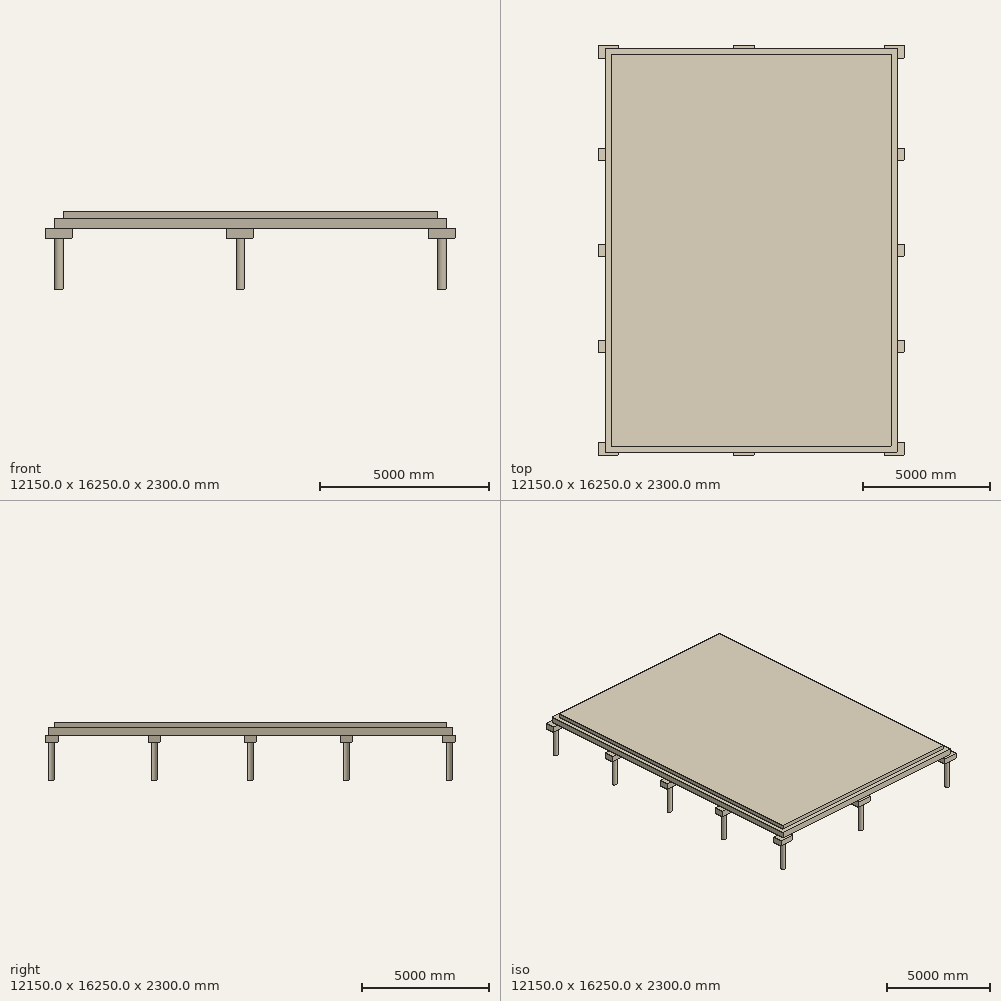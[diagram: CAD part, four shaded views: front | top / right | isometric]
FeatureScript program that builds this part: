
annotation { "Feature Type Name" : "Feature", "Feature Type Description" : "" }
export const myFeature = defineFeature(function(context is Context, id is Id, definition is map)
    precondition{}
    {
        {
            var Q0;
            Q0=qCreatedBy(makeId("Top.planeOp"),FACE);
            var sketch = newSketch(context, id + "F0", { "sketchPlane" : qUnion([Q0])});
            skLineSegment(sketch, "E0.bottom", {"start": v(5550, 7750) * mm, "end": v(-5550, 7750) * mm, "construction": true});
            skLineSegment(sketch, "E0.top", {"start": v(5550, -7750) * mm, "end": v(-5550, -7750) * mm, "construction": true});
            skLineSegment(sketch, "E0.left", {"start": v(5550, 7750) * mm, "end": v(5550, -7750) * mm, "construction": true});
            skLineSegment(sketch, "E0.right", {"start": v(-5550, 7750) * mm, "end": v(-5550, -7750) * mm, "construction": true});
            skPoint(sketch, "E0.middle", {"position": v(0, 0) * mm});
            skLineSegment(sketch, "E1", {"start": v(-300, -7750) * mm, "end": v(-300, 7750) * mm, "construction": true});
            skPoint(sketch, "E2", {"position": v(-5550, 0) * mm});
            skPoint(sketch, "E3", {"position": v(-5550, 3800) * mm});
            skPoint(sketch, "E4", {"position": v(-5550, -3800) * mm});
            skPoint(sketch, "E5", {"position": v(5550, -3800) * mm});
            skPoint(sketch, "E6", {"position": v(5550, 0) * mm});
            skPoint(sketch, "E7", {"position": v(5550, 3800) * mm});
            skLineSegment(sketch, "E8", {"start": v(900, 7750) * mm, "end": v(900, -7750) * mm, "construction": true});
            skLineSegment(sketch, "E9", {"start": v(5550, 3800) * mm, "end": v(900, 3800) * mm, "construction": true});
            skLineSegment(sketch, "E10", {"start": v(5550, 0) * mm, "end": v(900, 0) * mm, "construction": true});
            skLineSegment(sketch, "E11", {"start": v(5550, -3800) * mm, "end": v(900, -3800) * mm, "construction": true});
            skLineSegment(sketch, "E12", {"start": v(5550, 4900) * mm, "end": v(2550, 4900) * mm, "construction": true});
            skLineSegment(sketch, "E13", {"start": v(2550, 4900) * mm, "end": v(2550, 2700) * mm, "construction": true});
            skLineSegment(sketch, "E14", {"start": v(2550, -4900) * mm, "end": v(5550, -4900) * mm, "construction": true});
            skLineSegment(sketch, "E15", {"start": v(-4350, 7750) * mm, "end": v(-4350, 1750) * mm, "construction": true});
            skLineSegment(sketch, "E16", {"start": v(-4350, 1750) * mm, "end": v(-300, 1750) * mm, "construction": true});
            skLineSegment(sketch, "E17", {"start": v(-4350, 4750) * mm, "end": v(-3250, 4750) * mm, "construction": true});
            skLineSegment(sketch, "E18", {"start": v(-3250, 4750) * mm, "end": v(-3250, 7750) * mm, "construction": true});
            skLineSegment(sketch, "E19", {"start": v(-5550, 0) * mm, "end": v(-2550, 0) * mm, "construction": true});
            skLineSegment(sketch, "E20", {"start": v(-2550, 0) * mm, "end": v(-2550, -3800) * mm, "construction": true});
            skLineSegment(sketch, "E21", {"start": v(-2550, -3800) * mm, "end": v(-5550, -3800) * mm, "construction": true});
            skLineSegment(sketch, "E22", {"start": v(-5550, -2700) * mm, "end": v(-2550, -2700) * mm, "construction": true});
            skLineSegment(sketch, "E23", {"start": v(2550, 2700) * mm, "end": v(5550, 2700) * mm, "construction": true});
            skLineSegment(sketch, "E24", {"start": v(2550, -2700) * mm, "end": v(5550, -2700) * mm, "construction": true});
            skLineSegment(sketch, "E25.trimOffspring", {"start": v(2550, -2700) * mm, "end": v(2550, -4900) * mm, "construction": true});
            skPoint(sketch, "E26", {"position": v(-300, 0) * mm});
            skPoint(sketch, "E27", {"position": v(-300, 3800) * mm});
            skPoint(sketch, "E28", {"position": v(-300, -3800) * mm});
            skSolve(sketch);
        }
        {
            var Q0;
            Q0=qCreatedBy(makeId("Top.planeOp"),FACE);
            var sketch = newSketch(context, id + "F1", { "sketchPlane" : qUnion([Q0])});
            skLineSegment(sketch, "E29.0", {"start": v(5550, -7750) * mm, "end": v(-175, -7750) * mm});
            skLineSegment(sketch, "E30.0", {"start": v(-5550, 7750) * mm, "end": v(-5550, -7750) * mm});
            skLineSegment(sketch, "E31.0", {"start": v(5550, 7750) * mm, "end": v(-175, 7750) * mm});
            skLineSegment(sketch, "E32.0", {"start": v(5550, 7750) * mm, "end": v(5550, -7750) * mm});
            skLineSegment(sketch, "E33.0", {"start": v(-300, -7750) * mm, "end": v(-300, 7750) * mm, "construction": true});
            skLineSegment(sketch, "E34.0", {"start": v(5800, -8000) * mm, "end": v(-5800, -8000) * mm});
            skLineSegment(sketch, "E34.1", {"start": v(5800, 8000) * mm, "end": v(5800, -8000) * mm});
            skLineSegment(sketch, "E34.2", {"start": v(5800, 8000) * mm, "end": v(-5800, 8000) * mm});
            skLineSegment(sketch, "E34.3", {"start": v(-5800, 8000) * mm, "end": v(-5800, -8000) * mm});
            skLineSegment(sketch, "E35.left", {"start": v(-425, 7750) * mm, "end": v(-425, -7750) * mm});
            skLineSegment(sketch, "E35.right", {"start": v(-175, 7750) * mm, "end": v(-175, -7750) * mm});
            skPoint(sketch, "E35.middle", {"position": v(-300, 0) * mm});
            skLineSegment(sketch, "E36.trimOffspring", {"start": v(-425, -7750) * mm, "end": v(-5550, -7750) * mm});
            skLineSegment(sketch, "E37.trimOffspring", {"start": v(-425, 7750) * mm, "end": v(-5550, 7750) * mm});
            skLineSegment(sketch, "E38", {"start": v(-5800, -8000) * mm, "end": v(-5550, -7750) * mm, "construction": true});
            skPoint(sketch, "E39", {"position": v(-5675, -7875) * mm});
            skSolve(sketch);
        }
        {
            var Q0;
            Q0 = qSketchRegion(id + "F1", true);
            extrude(context, id + "F2", {"entities" : qUnion([Q0]), "oppositeDirection" : true, "depth" : 300 * mm});
        }
        {
            var Q0;
            Q0=makeQuery(id+"F2.opExtrude","CAP_FACE",FACE,{"disambiguationData":[OSD([sQuery(id+"F1.wireOp",EDGE,"E29.0"),sQuery(id+"F1.wireOp",EDGE,"E30.0"),sQuery(id+"F1.wireOp",EDGE,"E31.0"),sQuery(id+"F1.wireOp",EDGE,"E32.0"),sQuery(id+"F1.wireOp",EDGE,"E34.0"),sQuery(id+"F1.wireOp",EDGE,"E34.1"),sQuery(id+"F1.wireOp",EDGE,"E34.2"),sQuery(id+"F1.wireOp",EDGE,"E34.3"),sQuery(id+"F1.wireOp",EDGE,"E35.left"),sQuery(id+"F1.wireOp",EDGE,"E35.right"),sQuery(id+"F1.wireOp",EDGE,"E36.trimOffspring"),sQuery(id+"F1.wireOp",EDGE,"E37.trimOffspring")])],"isStart":false});
            var sketch = newSketch(context, id + "F3", { "sketchPlane" : qUnion([Q0])});
            skLineSegment(sketch, "E40", {"start": v(-5800, -8000) * mm, "end": v(-5550, -7750) * mm, "construction": true});
            skLineSegment(sketch, "E41", {"start": v(-175, -7750) * mm, "end": v(-425, -8000) * mm, "construction": true});
            skLineSegment(sketch, "E42", {"start": v(-425, 7750) * mm, "end": v(-175, 8000) * mm, "construction": true});
            skLineSegment(sketch, "E43", {"start": v(-5800, 8000) * mm, "end": v(-5550, 7750) * mm, "construction": true});
            skLineSegment(sketch, "E44", {"start": v(5800, 8000) * mm, "end": v(5550, 7750) * mm, "construction": true});
            skLineSegment(sketch, "E45", {"start": v(5550, -7750) * mm, "end": v(5800, -8000) * mm, "construction": true});
            skPoint(sketch, "E46.0", {"position": v(-5550, 0) * mm});
            skPoint(sketch, "E47.0", {"position": v(-5550, -3800) * mm});
            skPoint(sketch, "E48.0", {"position": v(-300, -3800) * mm});
            skPoint(sketch, "E49.0", {"position": v(-300, 0) * mm});
            skPoint(sketch, "E50.0", {"position": v(5550, -3800) * mm});
            skPoint(sketch, "E51.0", {"position": v(5550, 0) * mm});
            skPoint(sketch, "E52.0", {"position": v(5550, 3800) * mm});
            skPoint(sketch, "E53.0", {"position": v(-300, 3800) * mm});
            skPoint(sketch, "E54.0", {"position": v(-5550, 3800) * mm});
            skLineSegment(sketch, "E55", {"start": v(-5550, 3800) * mm, "end": v(-5800, 3800) * mm, "construction": true});
            skLineSegment(sketch, "E56", {"start": v(-5550, 0) * mm, "end": v(-5800, 0) * mm, "construction": true});
            skLineSegment(sketch, "E57", {"start": v(5550, 0) * mm, "end": v(5800, 0) * mm, "construction": true});
            skLineSegment(sketch, "E58", {"start": v(5550, 3800) * mm, "end": v(5800, 3800) * mm, "construction": true});
            skLineSegment(sketch, "E59", {"start": v(-5550, -3800) * mm, "end": v(-5800, -3800) * mm, "construction": true});
            skLineSegment(sketch, "E60", {"start": v(5550, -3800) * mm, "end": v(5800, -3800) * mm, "construction": true});
            skLineSegment(sketch, "E61.bottom", {"start": v(-5275, 8125) * mm, "end": v(-6075, 8125) * mm});
            skLineSegment(sketch, "E61.top", {"start": v(-5275, 7625) * mm, "end": v(-6075, 7625) * mm});
            skLineSegment(sketch, "E61.left", {"start": v(-5275, 8125) * mm, "end": v(-5275, 7625) * mm});
            skLineSegment(sketch, "E61.right", {"start": v(-6075, 8125) * mm, "end": v(-6075, 7625) * mm});
            skPoint(sketch, "E61.middle", {"position": v(-5675, 7875) * mm});
            skLineSegment(sketch, "E62.bottom", {"start": v(-5275, 4050) * mm, "end": v(-6075, 4050) * mm});
            skLineSegment(sketch, "E62.top", {"start": v(-5275, 3550) * mm, "end": v(-6075, 3550) * mm});
            skLineSegment(sketch, "E62.left", {"start": v(-5275, 4050) * mm, "end": v(-5275, 3550) * mm});
            skLineSegment(sketch, "E62.right", {"start": v(-6075, 4050) * mm, "end": v(-6075, 3550) * mm});
            skPoint(sketch, "E62.middle", {"position": v(-5675, 3800) * mm});
            skLineSegment(sketch, "E63.bottom", {"start": v(-5275, 250) * mm, "end": v(-6075, 250) * mm});
            skLineSegment(sketch, "E63.top", {"start": v(-5275, -250) * mm, "end": v(-6075, -250) * mm});
            skLineSegment(sketch, "E63.left", {"start": v(-5275, 250) * mm, "end": v(-5275, -250) * mm});
            skLineSegment(sketch, "E63.right", {"start": v(-6075, 250) * mm, "end": v(-6075, -250) * mm});
            skPoint(sketch, "E63.middle", {"position": v(-5675, 0) * mm});
            skLineSegment(sketch, "E64.bottom", {"start": v(-6075, -3550) * mm, "end": v(-5275, -3550) * mm});
            skLineSegment(sketch, "E64.top", {"start": v(-6075, -4050) * mm, "end": v(-5275, -4050) * mm});
            skLineSegment(sketch, "E64.left", {"start": v(-6075, -3550) * mm, "end": v(-6075, -4050) * mm});
            skLineSegment(sketch, "E64.right", {"start": v(-5275, -3550) * mm, "end": v(-5275, -4050) * mm});
            skPoint(sketch, "E64.middle", {"position": v(-5675, -3800) * mm});
            skLineSegment(sketch, "E65.bottom", {"start": v(-5275, -7625) * mm, "end": v(-6075, -7625) * mm});
            skLineSegment(sketch, "E65.top", {"start": v(-5275, -8125) * mm, "end": v(-6075, -8125) * mm});
            skLineSegment(sketch, "E65.left", {"start": v(-5275, -7625) * mm, "end": v(-5275, -8125) * mm});
            skLineSegment(sketch, "E65.right", {"start": v(-6075, -7625) * mm, "end": v(-6075, -8125) * mm});
            skPoint(sketch, "E65.middle", {"position": v(-5675, -7875) * mm});
            skLineSegment(sketch, "E66.bottom", {"start": v(100, 8125) * mm, "end": v(-700, 8125) * mm});
            skLineSegment(sketch, "E66.top", {"start": v(100, 7625) * mm, "end": v(-700, 7625) * mm});
            skLineSegment(sketch, "E66.left", {"start": v(100, 8125) * mm, "end": v(100, 7625) * mm});
            skLineSegment(sketch, "E66.right", {"start": v(-700, 8125) * mm, "end": v(-700, 7625) * mm});
            skPoint(sketch, "E66.middle", {"position": v(-300, 7875) * mm});
            skLineSegment(sketch, "E67.bottom", {"start": v(6075, 8125) * mm, "end": v(5275, 8125) * mm});
            skLineSegment(sketch, "E67.top", {"start": v(6075, 7625) * mm, "end": v(5275, 7625) * mm});
            skLineSegment(sketch, "E67.left", {"start": v(6075, 8125) * mm, "end": v(6075, 7625) * mm});
            skLineSegment(sketch, "E67.right", {"start": v(5275, 8125) * mm, "end": v(5275, 7625) * mm});
            skPoint(sketch, "E67.middle", {"position": v(5675, 7875) * mm});
            skLineSegment(sketch, "E68.bottom", {"start": v(100, 4050) * mm, "end": v(-700, 4050) * mm});
            skLineSegment(sketch, "E68.top", {"start": v(100, 3550) * mm, "end": v(-700, 3550) * mm});
            skLineSegment(sketch, "E68.left", {"start": v(100, 4050) * mm, "end": v(100, 3550) * mm});
            skLineSegment(sketch, "E68.right", {"start": v(-700, 4050) * mm, "end": v(-700, 3550) * mm});
            skLineSegment(sketch, "E69.bottom", {"start": v(6075, 4050) * mm, "end": v(5275, 4050) * mm});
            skLineSegment(sketch, "E69.top", {"start": v(6075, 3550) * mm, "end": v(5275, 3550) * mm});
            skLineSegment(sketch, "E69.left", {"start": v(6075, 4050) * mm, "end": v(6075, 3550) * mm});
            skLineSegment(sketch, "E69.right", {"start": v(5275, 4050) * mm, "end": v(5275, 3550) * mm});
            skPoint(sketch, "E69.middle", {"position": v(5675, 3800) * mm});
            skLineSegment(sketch, "E70.bottom", {"start": v(100, 250) * mm, "end": v(-700, 250) * mm});
            skLineSegment(sketch, "E70.top", {"start": v(100, -250) * mm, "end": v(-700, -250) * mm});
            skLineSegment(sketch, "E70.left", {"start": v(100, 250) * mm, "end": v(100, -250) * mm});
            skLineSegment(sketch, "E70.right", {"start": v(-700, 250) * mm, "end": v(-700, -250) * mm});
            skLineSegment(sketch, "E71.bottom", {"start": v(100, -3550) * mm, "end": v(-700, -3550) * mm});
            skLineSegment(sketch, "E71.top", {"start": v(100, -4050) * mm, "end": v(-700, -4050) * mm});
            skLineSegment(sketch, "E71.left", {"start": v(100, -3550) * mm, "end": v(100, -4050) * mm});
            skLineSegment(sketch, "E71.right", {"start": v(-700, -3550) * mm, "end": v(-700, -4050) * mm});
            skLineSegment(sketch, "E72.bottom", {"start": v(100, -7625) * mm, "end": v(-700, -7625) * mm});
            skLineSegment(sketch, "E72.top", {"start": v(100, -8125) * mm, "end": v(-700, -8125) * mm});
            skLineSegment(sketch, "E72.left", {"start": v(100, -7625) * mm, "end": v(100, -8125) * mm});
            skLineSegment(sketch, "E72.right", {"start": v(-700, -7625) * mm, "end": v(-700, -8125) * mm});
            skPoint(sketch, "E72.middle", {"position": v(-300, -7875) * mm});
            skLineSegment(sketch, "E73.bottom", {"start": v(6075, -7625) * mm, "end": v(5275, -7625) * mm});
            skLineSegment(sketch, "E73.top", {"start": v(6075, -8125) * mm, "end": v(5275, -8125) * mm});
            skLineSegment(sketch, "E73.left", {"start": v(6075, -7625) * mm, "end": v(6075, -8125) * mm});
            skLineSegment(sketch, "E73.right", {"start": v(5275, -7625) * mm, "end": v(5275, -8125) * mm});
            skPoint(sketch, "E73.middle", {"position": v(5675, -7875) * mm});
            skLineSegment(sketch, "E74.bottom", {"start": v(6075, -3550) * mm, "end": v(5275, -3550) * mm});
            skLineSegment(sketch, "E74.top", {"start": v(6075, -4050) * mm, "end": v(5275, -4050) * mm});
            skLineSegment(sketch, "E74.left", {"start": v(6075, -3550) * mm, "end": v(6075, -4050) * mm});
            skLineSegment(sketch, "E74.right", {"start": v(5275, -3550) * mm, "end": v(5275, -4050) * mm});
            skPoint(sketch, "E74.middle", {"position": v(5675, -3800) * mm});
            skLineSegment(sketch, "E75.bottom", {"start": v(6075, 250) * mm, "end": v(5275, 250) * mm});
            skLineSegment(sketch, "E75.top", {"start": v(6075, -250) * mm, "end": v(5275, -250) * mm});
            skLineSegment(sketch, "E75.left", {"start": v(6075, 250) * mm, "end": v(6075, -250) * mm});
            skLineSegment(sketch, "E75.right", {"start": v(5275, 250) * mm, "end": v(5275, -250) * mm});
            skPoint(sketch, "E75.middle", {"position": v(5675, 0) * mm});
            skSolve(sketch);
        }
        {
            var Q0;
            Q0 = qSketchRegion(id + "F3", true);
            extrude(context, id + "F4", {"entities" : qUnion([Q0]), "depth" : 300 * mm});
        }
        {
            var Q0;
            Q0=makeQuery(id+"F4.opExtrude","CAP_FACE",FACE,{"disambiguationData":[OSD([sQuery(id+"F3.wireOp",EDGE,"E61.bottom"),sQuery(id+"F3.wireOp",EDGE,"E61.top"),sQuery(id+"F3.wireOp",EDGE,"E61.left"),sQuery(id+"F3.wireOp",EDGE,"E61.right")])],"isStart":false});
            var sketch = newSketch(context, id + "F5", { "sketchPlane" : qUnion([Q0])});
            skPoint(sketch, "E76.0", {"position": v(-5675, -3800) * mm});
            skPoint(sketch, "E77.0", {"position": v(-5675, -7875) * mm});
            skPoint(sketch, "E78.0", {"position": v(-300, -7875) * mm});
            skPoint(sketch, "E79.0", {"position": v(-300, -3800) * mm});
            skPoint(sketch, "E80.0", {"position": v(5675, -3800) * mm});
            skPoint(sketch, "E81.0", {"position": v(5675, -7875) * mm});
            skPoint(sketch, "E82.0", {"position": v(5675, 0) * mm});
            skPoint(sketch, "E83.0", {"position": v(-300, 0) * mm});
            skPoint(sketch, "E84.0", {"position": v(-5675, 0) * mm});
            skPoint(sketch, "E85.0", {"position": v(-5675, 3800) * mm});
            skPoint(sketch, "E86.0", {"position": v(-300, 3800) * mm});
            skPoint(sketch, "E87.0", {"position": v(5675, 3800) * mm});
            skPoint(sketch, "E88.0", {"position": v(5675, 7875) * mm});
            skPoint(sketch, "E89.0", {"position": v(-5675, 7875) * mm});
            skPoint(sketch, "E90.0", {"position": v(-300, 7875) * mm});
            skCircle(sketch, "E91", {"center": v(-5675, 7875) * mm, "radius": 125 * mm});
            skCircle(sketch, "E92", {"center": v(-300, 7875) * mm, "radius": 125 * mm});
            skCircle(sketch, "E93", {"center": v(5675, 7875) * mm, "radius": 125 * mm});
            skCircle(sketch, "E94", {"center": v(-5675, 3800) * mm, "radius": 125 * mm});
            skCircle(sketch, "E95", {"center": v(-300, 3800) * mm, "radius": 125 * mm});
            skCircle(sketch, "E96", {"center": v(5675, 3800) * mm, "radius": 125 * mm});
            skCircle(sketch, "E97", {"center": v(-5675, 0) * mm, "radius": 125 * mm});
            skCircle(sketch, "E98", {"center": v(-300, 0) * mm, "radius": 125 * mm});
            skCircle(sketch, "E99", {"center": v(5675, 0) * mm, "radius": 125 * mm});
            skCircle(sketch, "E100", {"center": v(-5675, -3800) * mm, "radius": 125 * mm});
            skCircle(sketch, "E101", {"center": v(-300, -3800) * mm, "radius": 125 * mm});
            skCircle(sketch, "E102", {"center": v(5675, -3800) * mm, "radius": 125 * mm});
            skCircle(sketch, "E103", {"center": v(-5675, -7875) * mm, "radius": 125 * mm});
            skCircle(sketch, "E104", {"center": v(-300, -7875) * mm, "radius": 125 * mm});
            skCircle(sketch, "E105", {"center": v(5675, -7875) * mm, "radius": 125 * mm});
            skSolve(sketch);
        }
        {
            var Q0;
            Q0 = qSketchRegion(id + "F5", true);
            extrude(context, id + "F6", {"entities" : qUnion([Q0]), "depth" : 1500 * mm});
        }
        {
            var Q0;
            Q0=qCreatedBy(makeId("Top.planeOp"),FACE);
            var sketch = newSketch(context, id + "F7", { "sketchPlane" : qUnion([Q0])});
            skPoint(sketch, "E106.0", {"position": v(-5550, 7750) * mm});
            skPoint(sketch, "E107.0", {"position": v(5550, -7750) * mm});
            skLineSegment(sketch, "E108.bottom", {"start": v(-5550, 7750) * mm, "end": v(5550, 7750) * mm});
            skLineSegment(sketch, "E108.top", {"start": v(-5550, -7750) * mm, "end": v(5550, -7750) * mm});
            skLineSegment(sketch, "E108.left", {"start": v(-5550, 7750) * mm, "end": v(-5550, -7750) * mm});
            skLineSegment(sketch, "E108.right", {"start": v(5550, 7750) * mm, "end": v(5550, -7750) * mm});
            skSolve(sketch);
        }
        {
            var Q0;
            Q0=makeQuery(id+"F7.imprint","IMPRINT",FACE,{"disambiguationData":[TD([[makeQuery(id+"F7.imprint","IMPRINT",EDGE,{"derivedFrom":sQuery(id+"F7.wireOp",EDGE,"E108.bottom")}),-1.0]])]});
            extrude(context, id + "F8", {"entities" : qUnion([Q0]), "depth" : 200 * mm});
        }
    });
